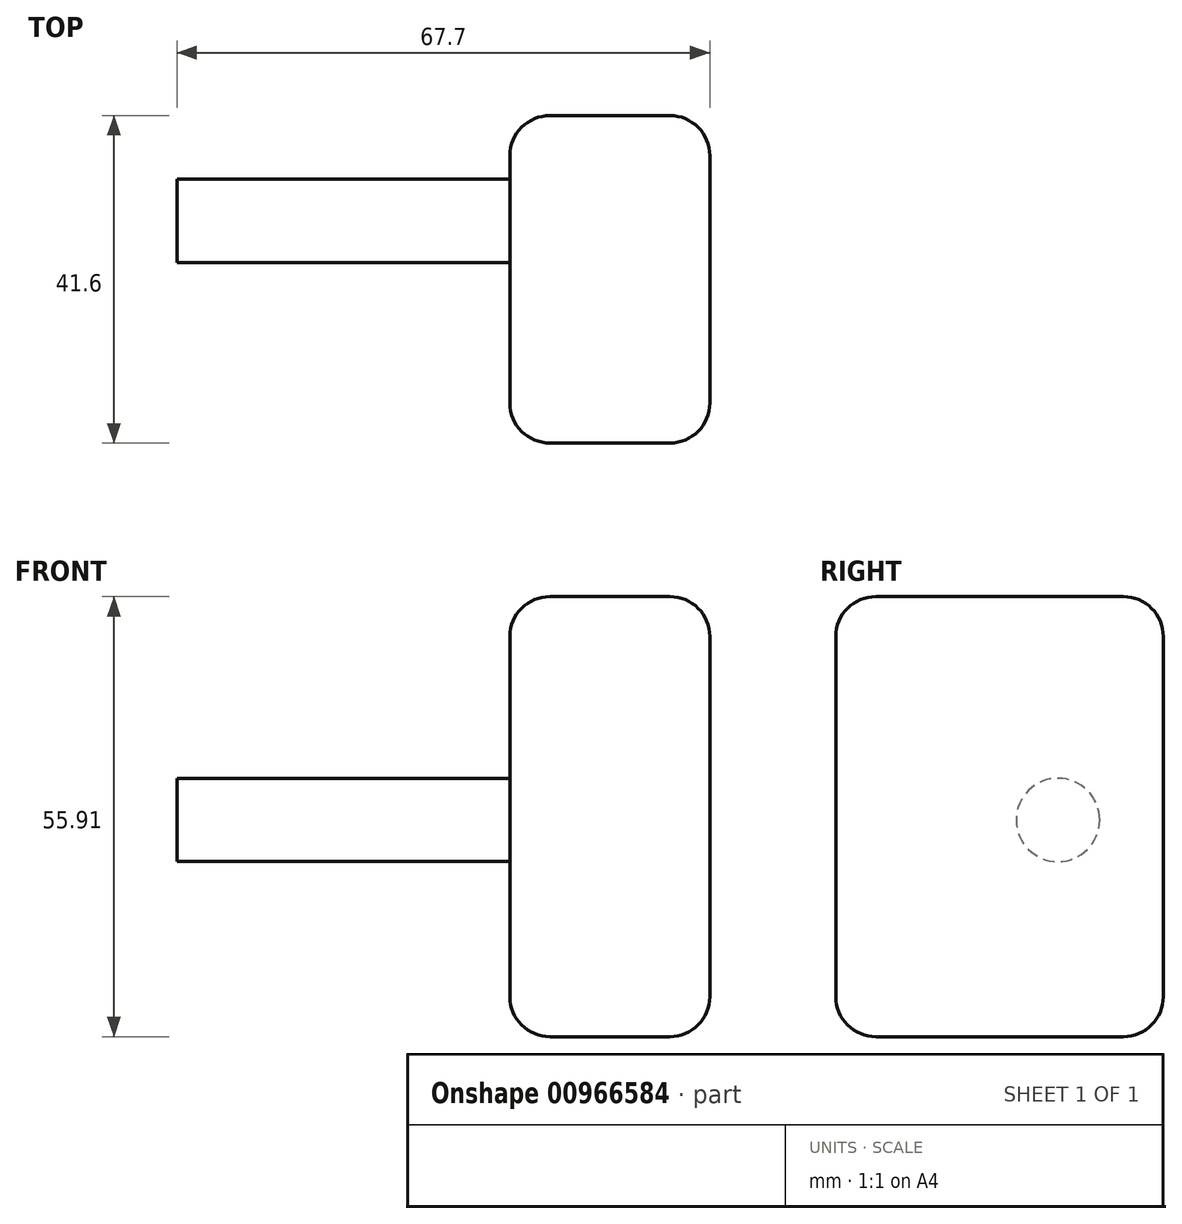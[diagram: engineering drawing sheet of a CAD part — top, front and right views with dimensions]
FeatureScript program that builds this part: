
annotation { "Feature Type Name" : "Feature", "Feature Type Description" : "" }
export const myFeature = defineFeature(function(context is Context, id is Id, definition is map)
    precondition{}
    {
        {
            var Q0;
            Q0=qCreatedBy(makeId("Right.planeOp"),FACE);
            var sketch = newSketch(context, id + "F0", { "sketchPlane" : qUnion([Q0])});
            skLineSegment(sketch, "E0.bottom", {"start": v(0, 0) * mm, "end": v(41.6, 0) * mm});
            skLineSegment(sketch, "E0.top", {"start": v(0, 55.9) * mm, "end": v(41.6, 55.9) * mm});
            skLineSegment(sketch, "E0.left", {"start": v(0, 0) * mm, "end": v(0, 55.9) * mm});
            skLineSegment(sketch, "E0.right", {"start": v(41.6, 0) * mm, "end": v(41.6, 55.9) * mm});
            skSolve(sketch);
        }
        {
            var Q0;
            Q0=makeQuery(id+"F0.imprint","IMPRINT",FACE,{"disambiguationData":[TD([[makeQuery(id+"F0.imprint","IMPRINT",EDGE,{"derivedFrom":sQuery(id+"F0.wireOp",EDGE,"E0.bottom")}),1.0]])]});
            var sketch = newSketch(context, id + "F1", { "sketchPlane" : qUnion([Q0])});
            skLineSegment(sketch, "E1.0", {"start": v(0, -12.7) * mm, "end": v(41.6, -12.7) * mm});
            skSolve(sketch);
        }
        {
            var Q0;
            Q0=makeQuery(id+"F1.imprint","IMPRINT",FACE,{"disambiguationData":[TD([[makeQuery(id+"F1.imprint","IMPRINT",EDGE,{"derivedFrom":makeQuery(id+"F0.imprint","IMPRINT",EDGE,{"derivedFrom":sQuery(id+"F0.wireOp",EDGE,"E0.bottom")})}),1.0]])]});
            var sketch = newSketch(context, id + "F2", { "sketchPlane" : qUnion([Q0])});
            skSolve(sketch);
        }
        {
            var Q0;
            Q0=makeQuery(id+"F2.imprint","IMPRINT",FACE,{"disambiguationData":[TD([[makeQuery(id+"F2.imprint","IMPRINT",EDGE,{"derivedFrom":makeQuery(id+"F1.imprint","IMPRINT",EDGE,{"derivedFrom":makeQuery(id+"F0.imprint","IMPRINT",EDGE,{"derivedFrom":sQuery(id+"F0.wireOp",EDGE,"E0.bottom")})})}),1.0]])]});
            extrude(context, id + "F3", {"entities" : qUnion([Q0]), "depth" : 25.4 * mm, "offsetDistance" : 25.4 * mm});
        }
        {
            var Q0;
            Q0=makeQuery(id+"F3.opExtrude","SWEPT_FACE",FACE,{"disambiguationData":[OSD([sQuery(id+"F0.wireOp",EDGE,"E0.bottom")])]});
            var Q1;
            Q1=makeQuery(id+"F3.opExtrude","CAP_FACE",FACE,{"disambiguationData":[OSD([sQuery(id+"F0.wireOp",EDGE,"E0.bottom"),sQuery(id+"F0.wireOp",EDGE,"E0.top"),sQuery(id+"F0.wireOp",EDGE,"E0.left"),sQuery(id+"F0.wireOp",EDGE,"E0.right")])],"isStart":false});
            var Q2;
            Q2=makeQuery(id+"F3.opExtrude","SWEPT_FACE",FACE,{"disambiguationData":[OSD([sQuery(id+"F0.wireOp",EDGE,"E0.right")])]});
            fillet(context, id + "F4", {"entities" : qUnion([Q0, Q1, Q2]), "radius" : 5.08 * mm, "tangentPropagation" : true, "allowEdgeOverflow" : false});
        }
        {
            var Q0;
            Q0=makeQuery(id+"F3.opExtrude","CAP_EDGE",EDGE,{"disambiguationData":[OSD([sQuery(id+"F0.wireOp",EDGE,"E0.left")])],"isStart":true});
            var Q1;
            Q1=makeQuery(id+"F3.opExtrude","CAP_EDGE",EDGE,{"disambiguationData":[OSD([sQuery(id+"F0.wireOp",EDGE,"E0.top")])],"isStart":true});
            var Q2;
            Q2=makeQuery(id+"F3.opExtrude","SWEPT_EDGE",EDGE,{"disambiguationData":[OSD([sQuery(id+"F0.wireOp",EDGE,"E0.top"),sQuery(id+"F0.wireOp",EDGE,"E0.left")])]});
            fillet(context, id + "F5", {"entities" : qUnion([Q0, Q1, Q2]), "radius" : 5.08 * mm, "tangentPropagation" : true, "allowEdgeOverflow" : false});
        }
        {
            var Q0;
            Q0=makeQuery(id+"F3.opExtrude","CAP_FACE",FACE,{"disambiguationData":[OSD([sQuery(id+"F0.wireOp",EDGE,"E0.bottom"),sQuery(id+"F0.wireOp",EDGE,"E0.top"),sQuery(id+"F0.wireOp",EDGE,"E0.left"),sQuery(id+"F0.wireOp",EDGE,"E0.right")])],"isStart":false});
            var sketch = newSketch(context, id + "F6", { "sketchPlane" : qUnion([Q0])});
            skCircle(sketch, "E2", {"center": v(26.77, 28.34) * mm, "radius": 4.56 * mm});
            skCircle(sketch, "E3", {"center": v(18.04, 21.97) * mm, "radius": 10.8 * mm});
            skSolve(sketch);
        }
        {
            var Q0;
            Q0 = qSketchRegion(id + "F6", true);
            extrude(context, id + "F7", {"entities" : qUnion([Q0]), "operationType" : NewBodyOperationType.REMOVE, "depth" : 25.4 * mm, "offsetDistance" : 25.4 * mm});
        }
        {
            var Q0;
            Q0=makeQuery(id+"F3.opExtrude","CAP_FACE",FACE,{"disambiguationData":[OSD([sQuery(id+"F0.wireOp",EDGE,"E0.bottom"),sQuery(id+"F0.wireOp",EDGE,"E0.top"),sQuery(id+"F0.wireOp",EDGE,"E0.left"),sQuery(id+"F0.wireOp",EDGE,"E0.right")])],"isStart":false});
            var sketch = newSketch(context, id + "F8", { "sketchPlane" : qUnion([Q0])});
            skCircle(sketch, "E4", {"center": v(28.22, 27.53) * mm, "radius": 5.3 * mm});
            skSolve(sketch);
        }
        {
            var Q0;
            Q0 = qSketchRegion(id + "F8", true);
            extrude(context, id + "F9", {"entities" : qUnion([Q0]), "operationType" : NewBodyOperationType.ADD, "oppositeDirection" : true, "depth" : 67.7 * mm, "offsetDistance" : 25.4 * mm});
        }
    });
